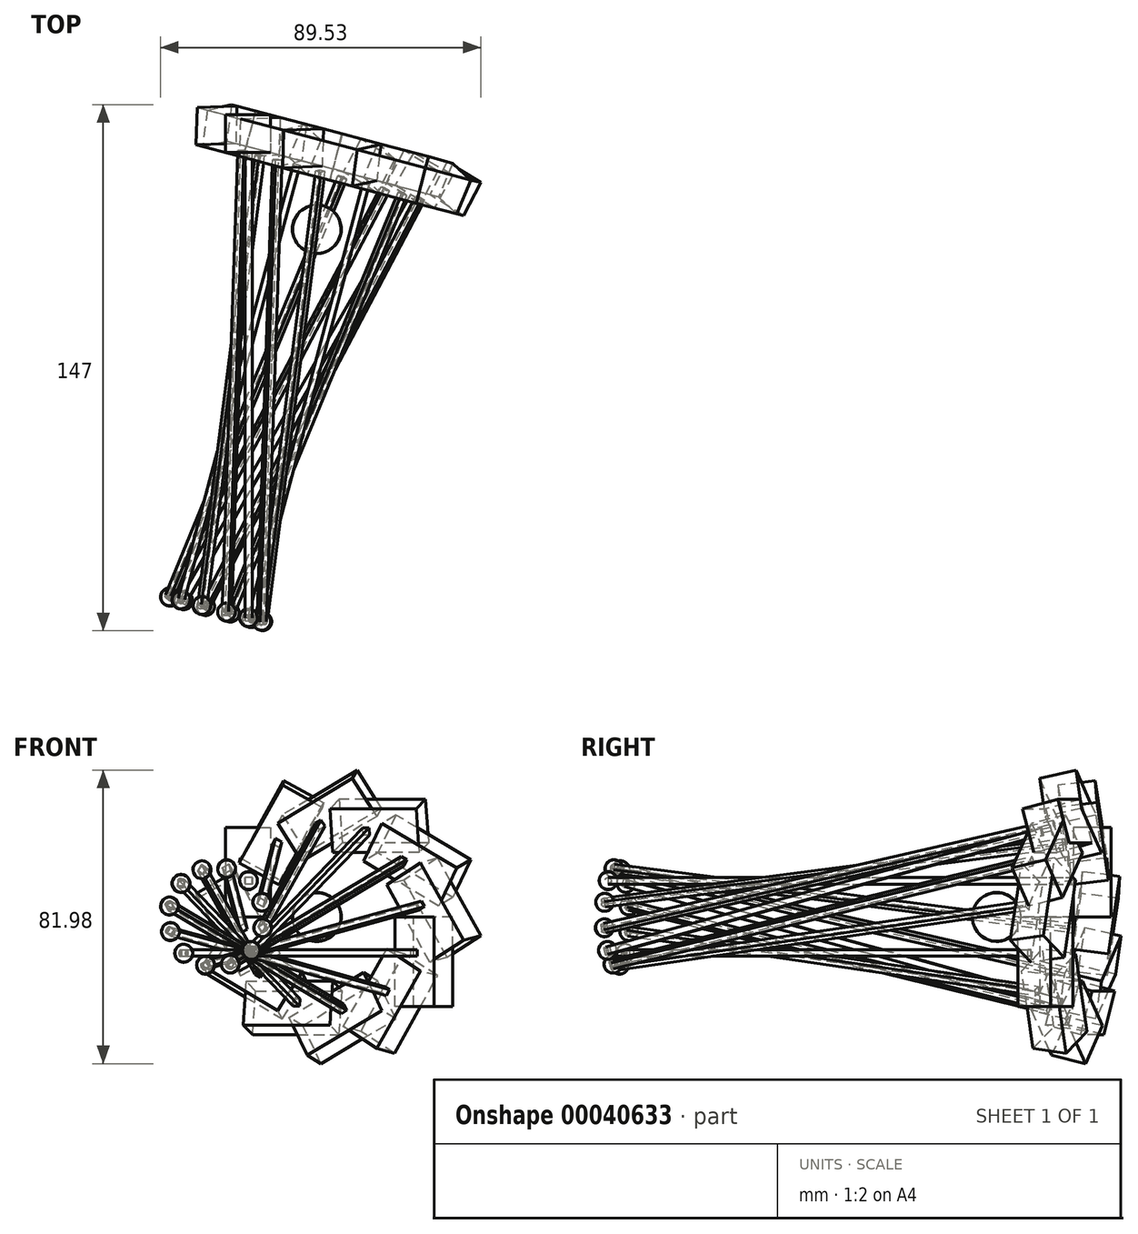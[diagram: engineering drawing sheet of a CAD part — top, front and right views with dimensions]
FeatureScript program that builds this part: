
annotation { "Feature Type Name" : "Feature", "Feature Type Description" : "" }
export const myFeature = defineFeature(function(context is Context, id is Id, definition is map)
    precondition{}
    {
        {
            var Q0;
            Q0=qCreatedBy(makeId("Top.planeOp"),FACE);
            var sketch = newSketch(context, id + "F0", { "sketchPlane" : qUnion([Q0])});
            skLineSegment(sketch, "E0.bottom", {"start": v(-25.61, 31.94) * mm, "end": v(-12.96, 31.94) * mm});
            skLineSegment(sketch, "E0.top", {"start": v(-25.61, 21.42) * mm, "end": v(-12.96, 21.42) * mm});
            skLineSegment(sketch, "E0.left", {"start": v(-25.61, 31.94) * mm, "end": v(-25.61, 21.42) * mm});
            skLineSegment(sketch, "E0.right", {"start": v(-12.96, 31.94) * mm, "end": v(-12.96, 21.42) * mm});
            skCircle(sketch, "E1", {"center": v(0, 0) * mm, "radius": 6.8 * mm});
            skLineSegment(sketch, "E2", {"start": v(1.7, 6.58) * mm, "end": v(-1.79, -6.56) * mm});
            skSolve(sketch);
        }
        {
            var Q0;
            Q0=makeQuery(id+"F0.imprint","IMPRINT",FACE,{"disambiguationData":[TD([[makeQuery(id+"F0.imprint","IMPRINT",EDGE,{"derivedFrom":sQuery(id+"F0.wireOp",EDGE,"E0.bottom")}),-1.0]])]});
            extrude(context, id + "F1", {"entities" : qUnion([Q0]), "depth" : 25 * mm});
        }
        {
            var Q0;
            {var subQ0=sQuery(id+"F0.wireOp",EDGE,"E2");Q0=makeQuery(id+"F0.imprint","IMPRINT",FACE,{"disambiguationData":[TD([[makeQuery(id+"F0.imprint","IMPRINT",EDGE,{"derivedFrom":subQ0}),-1.0]])]});}
            var Q1;
            Q1=sQuery(id+"F0.wireOp",EDGE,"E2");
            revolve(context, id + "F2", {"entities" : qUnion([Q0]), "axis" : qUnion([Q1]), "revolveType" : RevolveType.FULL});
        }
        {
            var Q0;
            Q0=makeQuery(id+"F1.opExtrude","SWEPT_BODY",BODY,{"disambiguationData":[OSD([sQuery(id+"F0.wireOp",EDGE,"E0.bottom"),sQuery(id+"F0.wireOp",EDGE,"E0.top"),sQuery(id+"F0.wireOp",EDGE,"E0.left"),sQuery(id+"F0.wireOp",EDGE,"E0.right")])]});
            var Q1;
            Q1=makeQuery(id+"F2.opRevolve","SWEPT_FACE",FACE,{"disambiguationData":[OSD([sQuery(id+"F0.wireOp",EDGE,"E1")])]});
            circularPattern(context, id + "F3", {"entities" : qUnion([Q0]), "axis" : qUnion([Q1]), "angle" : 30 * degree, "instanceCount" : 12});
        }
        {
            var Q0;
            Q0=makeQuery(id+"F3.opPattern","COPY",FACE,{"derivedFrom":makeQuery(id+"F1.opExtrude","SWEPT_FACE",FACE,{"disambiguationData":[OSD([sQuery(id+"F0.wireOp",EDGE,"E0.top")])]}),"instanceName":"6"});
            var sketch = newSketch(context, id + "F4", { "sketchPlane" : qUnion([Q0])});
            skLineSegment(sketch, "E3.bottom", {"start": v(17.97, -11) * mm, "end": v(19.99, -11) * mm});
            skLineSegment(sketch, "E3.top", {"start": v(17.97, -9.17) * mm, "end": v(19.99, -9.17) * mm});
            skLineSegment(sketch, "E3.left", {"start": v(17.97, -11) * mm, "end": v(17.97, -9.17) * mm});
            skLineSegment(sketch, "E3.right", {"start": v(19.99, -11) * mm, "end": v(19.99, -9.17) * mm});
            skSolve(sketch);
        }
        {
            var Q0;
            Q0=makeQuery(id+"F4.imprint","IMPRINT",FACE,{"disambiguationData":[TD([[makeQuery(id+"F4.imprint","IMPRINT",EDGE,{"derivedFrom":sQuery(id+"F4.wireOp",EDGE,"E3.bottom")}),1.0]])]});
            extrude(context, id + "F5", {"entities" : qUnion([Q0]), "depth" : 130 * mm});
        }
        {
            var Q0;
            Q0=makeQuery(id+"F5.opExtrude","SWEPT_BODY",BODY,{"disambiguationData":[OSD([sQuery(id+"F4.wireOp",EDGE,"E3.bottom"),sQuery(id+"F4.wireOp",EDGE,"E3.top"),sQuery(id+"F4.wireOp",EDGE,"E3.left"),sQuery(id+"F4.wireOp",EDGE,"E3.right")])]});
            var Q1;
            Q1=makeQuery(id+"F2.opRevolve","SWEPT_FACE",FACE,{"disambiguationData":[OSD([sQuery(id+"F0.wireOp",EDGE,"E1")])]});
            circularPattern(context, id + "F6", {"entities" : qUnion([Q0]), "axis" : qUnion([Q1]), "angle" : 30 * degree, "instanceCount" : 12});
        }
        {
            var Q0;
            Q0=makeQuery(id+"F6.opPattern","COPY",FACE,{"derivedFrom":makeQuery(id+"F5.opExtrude","CAP_FACE",FACE,{"disambiguationData":[OSD([sQuery(id+"F4.wireOp",EDGE,"E3.bottom"),sQuery(id+"F4.wireOp",EDGE,"E3.top"),sQuery(id+"F4.wireOp",EDGE,"E3.left"),sQuery(id+"F4.wireOp",EDGE,"E3.right")])],"isStart":false}),"instanceName":"4"});
            var sketch = newSketch(context, id + "F7", { "sketchPlane" : qUnion([Q0])});
            skCircle(sketch, "E4", {"center": v(-18.83, -10.67) * mm, "radius": 2.5 * mm});
            skLineSegment(sketch, "E5", {"start": v(-20.23, -12.74) * mm, "end": v(-17.48, -8.57) * mm});
            skSolve(sketch);
        }
        {
            var Q0;
            {var subQ3=makeQuery(id+"F6.opPattern","COPY",EDGE,{"derivedFrom":makeQuery(id+"F5.opExtrude","CAP_EDGE",EDGE,{"disambiguationData":[OSD([sQuery(id+"F4.wireOp",EDGE,"E3.bottom")])],"isStart":false}),"instanceName":"4"});Q0=makeQuery(id+"F7.imprint","IMPRINT",FACE,{"disambiguationData":[TD([[makeQuery(id+"F7.imprint","IMPRINT",EDGE,{"derivedFrom":subQ3}),-1.0]])]});}
            var Q1;
            Q1=sQuery(id+"F7.wireOp",EDGE,"E5");
            revolve(context, id + "F8", {"entities" : qUnion([Q0]), "axis" : qUnion([Q1]), "revolveType" : RevolveType.FULL});
        }
        {
            var Q0;
            Q0=makeQuery(id+"F8.opRevolve","SWEPT_BODY",BODY,{"disambiguationData":[OSD([sQuery(id+"F4.wireOp",EDGE,"E3.bottom"),sQuery(id+"F4.wireOp",EDGE,"E3.left"),sQuery(id+"F4.wireOp",EDGE,"E3.right"),sQuery(id+"F7.wireOp",EDGE,"E4"),sQuery(id+"F7.wireOp",EDGE,"E5")])]});
            var Q1;
            Q1=makeQuery(id+"F2.opRevolve","SWEPT_FACE",FACE,{"disambiguationData":[OSD([sQuery(id+"F0.wireOp",EDGE,"E1")])]});
            circularPattern(context, id + "F9", {"entities" : qUnion([Q0]), "axis" : qUnion([Q1]), "angle" : 30 * degree, "instanceCount" : 12});
        }
    });
